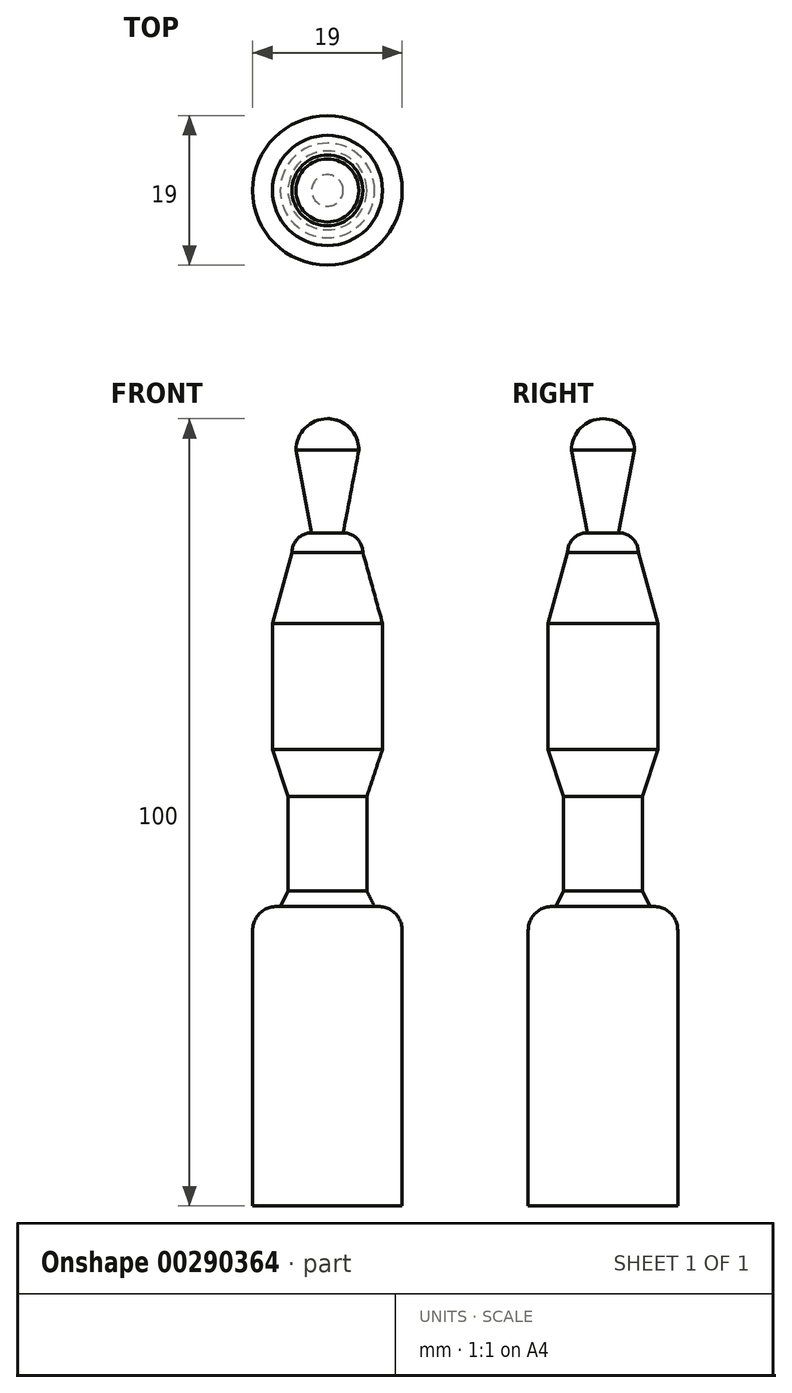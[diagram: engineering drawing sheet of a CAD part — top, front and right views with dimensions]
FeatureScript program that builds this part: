
annotation { "Feature Type Name" : "Feature", "Feature Type Description" : "" }
export const myFeature = defineFeature(function(context is Context, id is Id, definition is map)
    precondition{}
    {
        {
            var Q0;
            Q0=qCreatedBy(makeId("Front.planeOp"),FACE);
            var sketch = newSketch(context, id + "F0", { "sketchPlane" : qUnion([Q0])});
            skLineSegment(sketch, "E0", {"start": v(4, -4) * mm, "end": v(2, -14.5) * mm});
            skArc(sketch, "E1", {"start": v(4.5, -17) * mm, "mid": v(3.77, -15.23) * mm, "end": v(2, -14.5) * mm});
            skLineSegment(sketch, "E2", {"start": v(4.5, -17) * mm, "end": v(7, -26) * mm});
            skLineSegment(sketch, "E3", {"start": v(7, -26) * mm, "end": v(7, -42) * mm});
            skLineSegment(sketch, "E4", {"start": v(7, -42) * mm, "end": v(5, -48) * mm});
            skLineSegment(sketch, "E5", {"start": v(5, -48) * mm, "end": v(5, -60) * mm});
            skLineSegment(sketch, "E6", {"start": v(5, -60) * mm, "end": v(6, -62) * mm});
            skLineSegment(sketch, "E7", {"start": v(9.5, -65) * mm, "end": v(9.5, -100) * mm});
            skLineSegment(sketch, "E8", {"start": v(9.5, -100) * mm, "end": v(0, -100) * mm});
            skLineSegment(sketch, "E9", {"start": v(0, -100) * mm, "end": v(0, 0) * mm});
            skArc(sketch, "E10", {"start": v(9.5, -65) * mm, "mid": v(8.44, -62.7) * mm, "end": v(6, -62) * mm});
            skArc(sketch, "E11", {"start": v(4, -4) * mm, "mid": v(2.83, -1.17) * mm, "end": v(0, 0) * mm});
            skSolve(sketch);
        }
        {
            var Q0;
            Q0=sQuery(id+"F0.wireOp",EDGE,"E8");
            var Q1;
            Q1=sQuery(id+"F0.wireOp",EDGE,"E7");
            var Q2;
            Q2=sQuery(id+"F0.wireOp",EDGE,"E10");
            var Q3;
            Q3=sQuery(id+"F0.wireOp",EDGE,"E6");
            var Q4;
            Q4=sQuery(id+"F0.wireOp",EDGE,"E5");
            var Q5;
            Q5=sQuery(id+"F0.wireOp",EDGE,"E4");
            var Q6;
            Q6=sQuery(id+"F0.wireOp",EDGE,"E3");
            var Q7;
            Q7=sQuery(id+"F0.wireOp",EDGE,"E2");
            var Q8;
            Q8=sQuery(id+"F0.wireOp",EDGE,"E1");
            var Q9;
            Q9=sQuery(id+"F0.wireOp",EDGE,"E0");
            var Q10;
            Q10=sQuery(id+"F0.wireOp",EDGE,"E11");
            var Q11;
            Q11=sQuery(id+"F0.wireOp",EDGE,"E9");
            revolve(context, id + "F1", {"bodyType" : ToolBodyType.SURFACE, "surfaceEntities" : qUnion([Q0, Q1, Q2, Q3, Q4, Q5, Q6, Q7, Q8, Q9, Q10]), "axis" : qUnion([Q11]), "revolveType" : RevolveType.FULL});
        }
    });
